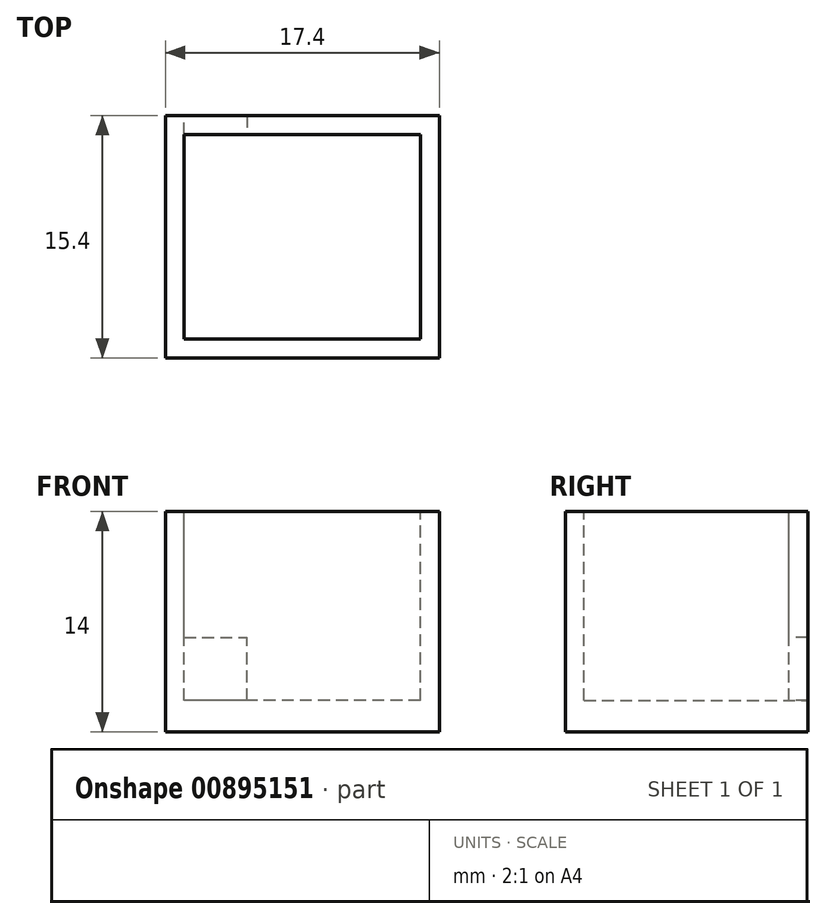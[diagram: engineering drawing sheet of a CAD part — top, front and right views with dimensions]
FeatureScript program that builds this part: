
annotation { "Feature Type Name" : "Feature", "Feature Type Description" : "" }
export const myFeature = defineFeature(function(context is Context, id is Id, definition is map)
    precondition{}
    {
        {
            var Q0;
            Q0=qCreatedBy(makeId("Top.planeOp"),FACE);
            var sketch = newSketch(context, id + "F0", { "sketchPlane" : qUnion([Q0])});
            skLineSegment(sketch, "E0.bottom", {"start": v(8.7, -7.7) * mm, "end": v(-8.7, -7.7) * mm});
            skLineSegment(sketch, "E0.top", {"start": v(8.7, 7.7) * mm, "end": v(-8.7, 7.7) * mm});
            skLineSegment(sketch, "E0.left", {"start": v(8.7, -7.7) * mm, "end": v(8.7, 7.7) * mm});
            skLineSegment(sketch, "E0.right", {"start": v(-8.7, -7.7) * mm, "end": v(-8.7, 7.7) * mm});
            skPoint(sketch, "E0.middle", {"position": v(0, 0) * mm});
            skSolve(sketch);
        }
        {
            var Q0;
            Q0 = qSketchRegion(id + "F0", true);
            extrude(context, id + "F1", {"entities" : qUnion([Q0]), "depth" : 14 * mm, "offsetDistance" : 25 * mm});
        }
        {
            var Q0;
            Q0=makeQuery(id+"F1.opExtrude","CAP_FACE",FACE,{"disambiguationData":[OSD([sQuery(id+"F0.wireOp",EDGE,"E0.bottom"),sQuery(id+"F0.wireOp",EDGE,"E0.top"),sQuery(id+"F0.wireOp",EDGE,"E0.left"),sQuery(id+"F0.wireOp",EDGE,"E0.right")])],"isStart":false});
            var sketch = newSketch(context, id + "F2", { "sketchPlane" : qUnion([Q0])});
            skLineSegment(sketch, "E1.bottom", {"start": v(7.5, -6.5) * mm, "end": v(-7.5, -6.5) * mm});
            skLineSegment(sketch, "E1.top", {"start": v(7.5, 6.5) * mm, "end": v(-7.5, 6.5) * mm});
            skLineSegment(sketch, "E1.left", {"start": v(7.5, -6.5) * mm, "end": v(7.5, 6.5) * mm});
            skLineSegment(sketch, "E1.right", {"start": v(-7.5, -6.5) * mm, "end": v(-7.5, 6.5) * mm});
            skPoint(sketch, "E1.middle", {"position": v(0, 0) * mm});
            skSolve(sketch);
        }
        {
            var Q0;
            Q0 = qSketchRegion(id + "F2", true);
            extrude(context, id + "F3", {"entities" : qUnion([Q0]), "operationType" : NewBodyOperationType.REMOVE, "oppositeDirection" : true, "depth" : 12 * mm, "offsetDistance" : 25 * mm});
        }
        {
            var Q0;
            Q0=makeQuery(id+"F3.boolean.opBoolean","COPY",FACE,{"derivedFrom":makeQuery(id+"F3.opExtrude","SWEPT_FACE",FACE,{"disambiguationData":[OSD([sQuery(id+"F2.wireOp",EDGE,"E1.top")])]})});
            var sketch = newSketch(context, id + "F4", { "sketchPlane" : qUnion([Q0])});
            skLineSegment(sketch, "E2.bottom", {"start": v(-7.5, 2) * mm, "end": v(-3.5, 2) * mm});
            skLineSegment(sketch, "E2.top", {"start": v(-7.5, 6) * mm, "end": v(-3.5, 6) * mm});
            skLineSegment(sketch, "E2.left", {"start": v(-7.5, 2) * mm, "end": v(-7.5, 6) * mm});
            skLineSegment(sketch, "E2.right", {"start": v(-3.5, 2) * mm, "end": v(-3.5, 6) * mm});
            skSolve(sketch);
        }
        {
            var Q0;
            Q0 = qSketchRegion(id + "F4", true);
            extrude(context, id + "F5", {"entities" : qUnion([Q0]), "operationType" : NewBodyOperationType.REMOVE, "oppositeDirection" : true, "depth" : 1.2 * mm, "offsetDistance" : 25 * mm});
        }
    });
